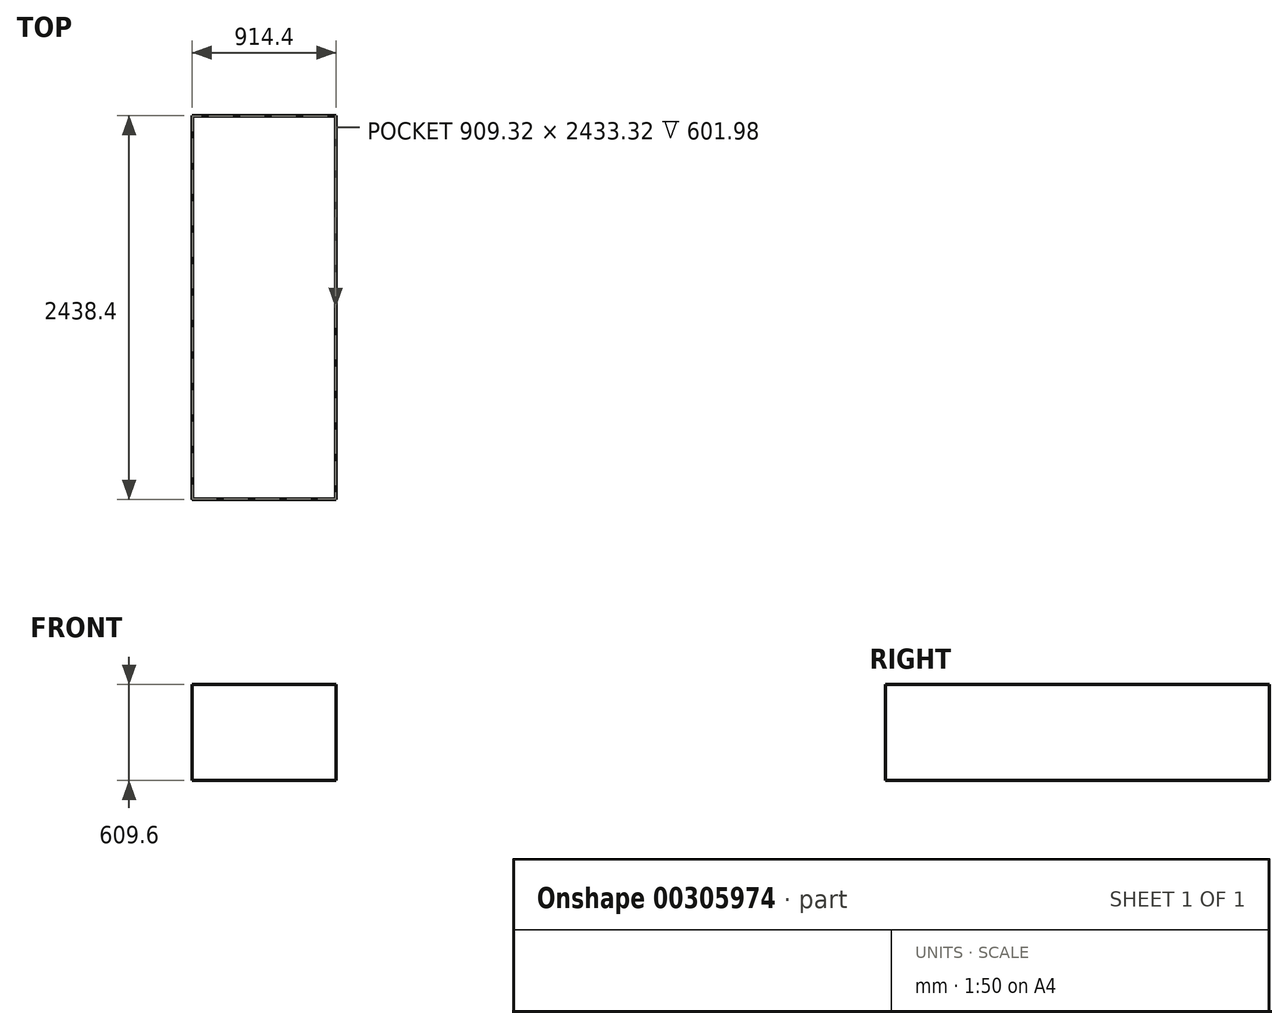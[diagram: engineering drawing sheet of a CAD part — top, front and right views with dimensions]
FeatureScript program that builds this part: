
annotation { "Feature Type Name" : "Feature", "Feature Type Description" : "" }
export const myFeature = defineFeature(function(context is Context, id is Id, definition is map)
    precondition{}
    {
        {
            var Q0;
            Q0=qCreatedBy(makeId("Top.planeOp"),FACE);
            var sketch = newSketch(context, id + "F0", { "sketchPlane" : qUnion([Q0])});
            skLineSegment(sketch, "E0.bottom", {"start": v(-700.26, -824.21) * mm, "end": v(214.14, -824.21) * mm});
            skLineSegment(sketch, "E0.top", {"start": v(-700.26, 1614.19) * mm, "end": v(214.14, 1614.19) * mm});
            skLineSegment(sketch, "E0.left", {"start": v(-700.26, -824.21) * mm, "end": v(-700.26, 1614.19) * mm});
            skLineSegment(sketch, "E0.right", {"start": v(214.14, -824.21) * mm, "end": v(214.14, 1614.19) * mm});
            skSolve(sketch);
        }
        {
            var Q0;
            Q0 = qSketchRegion(id + "F0", true);
            extrude(context, id + "F1", {"entities" : qUnion([Q0]), "depth" : 609.6 * mm});
        }
        {
            var Q0;
            Q0=makeQuery(id+"F1.opExtrude","CAP_FACE",FACE,{"disambiguationData":[OSD([sQuery(id+"F0.wireOp",EDGE,"E0.bottom"),sQuery(id+"F0.wireOp",EDGE,"E0.top"),sQuery(id+"F0.wireOp",EDGE,"E0.left"),sQuery(id+"F0.wireOp",EDGE,"E0.right")])],"isStart":false});
            var sketch = newSketch(context, id + "F2", { "sketchPlane" : qUnion([Q0])});
            skLineSegment(sketch, "E1.0", {"start": v(-693.91, 1607.84) * mm, "end": v(207.79, 1607.84) * mm});
            skLineSegment(sketch, "E1.1", {"start": v(-693.91, -817.86) * mm, "end": v(-693.91, 1607.84) * mm});
            skLineSegment(sketch, "E1.2", {"start": v(-693.91, -817.86) * mm, "end": v(207.79, -817.86) * mm});
            skLineSegment(sketch, "E1.3", {"start": v(207.79, -817.86) * mm, "end": v(207.79, 1607.84) * mm});
            skSolve(sketch);
        }
        {
            var Q0;
            Q0=makeQuery(id+"F1.opExtrude","CAP_FACE",FACE,{"disambiguationData":[OSD([sQuery(id+"F0.wireOp",EDGE,"E0.bottom"),sQuery(id+"F0.wireOp",EDGE,"E0.top"),sQuery(id+"F0.wireOp",EDGE,"E0.left"),sQuery(id+"F0.wireOp",EDGE,"E0.right")])],"isStart":false});
            shell(context, id + "F3", {"entities" : qUnion([Q0]), "thickness" : 2.54 * mm});
        }
        {
            var Q0;
            {var subQ0=sQuery(id+"F0.wireOp",EDGE,"E0.left");Q0=makeQuery(id+"F3.opShell","OFFSET_EDGE",EDGE,{"disambiguationData":[OSD([subQ0]),TDD([makeQuery(id+"F1.opExtrude","CAP_EDGE",EDGE,{"disambiguationData":[OSD([subQ0])],"isStart":false})])]});}
            var Q1;
            {var subQ0=sQuery(id+"F0.wireOp",EDGE,"E0.bottom");Q1=makeQuery(id+"F3.opShell","OFFSET_EDGE",EDGE,{"disambiguationData":[OSD([subQ0]),TDD([makeQuery(id+"F1.opExtrude","CAP_EDGE",EDGE,{"disambiguationData":[OSD([subQ0])],"isStart":false})])]});}
            var Q2;
            {var subQ0=sQuery(id+"F0.wireOp",EDGE,"E0.top");Q2=makeQuery(id+"F3.opShell","OFFSET_EDGE",EDGE,{"disambiguationData":[OSD([subQ0]),TDD([makeQuery(id+"F1.opExtrude","CAP_EDGE",EDGE,{"disambiguationData":[OSD([subQ0])],"isStart":false})])]});}
            fillet(context, id + "F4", {"entities" : qUnion([Q0, Q1, Q2]), "radius" : 5.08 * mm, "tangentPropagation" : true, "allowEdgeOverflow" : false});
        }
    });
